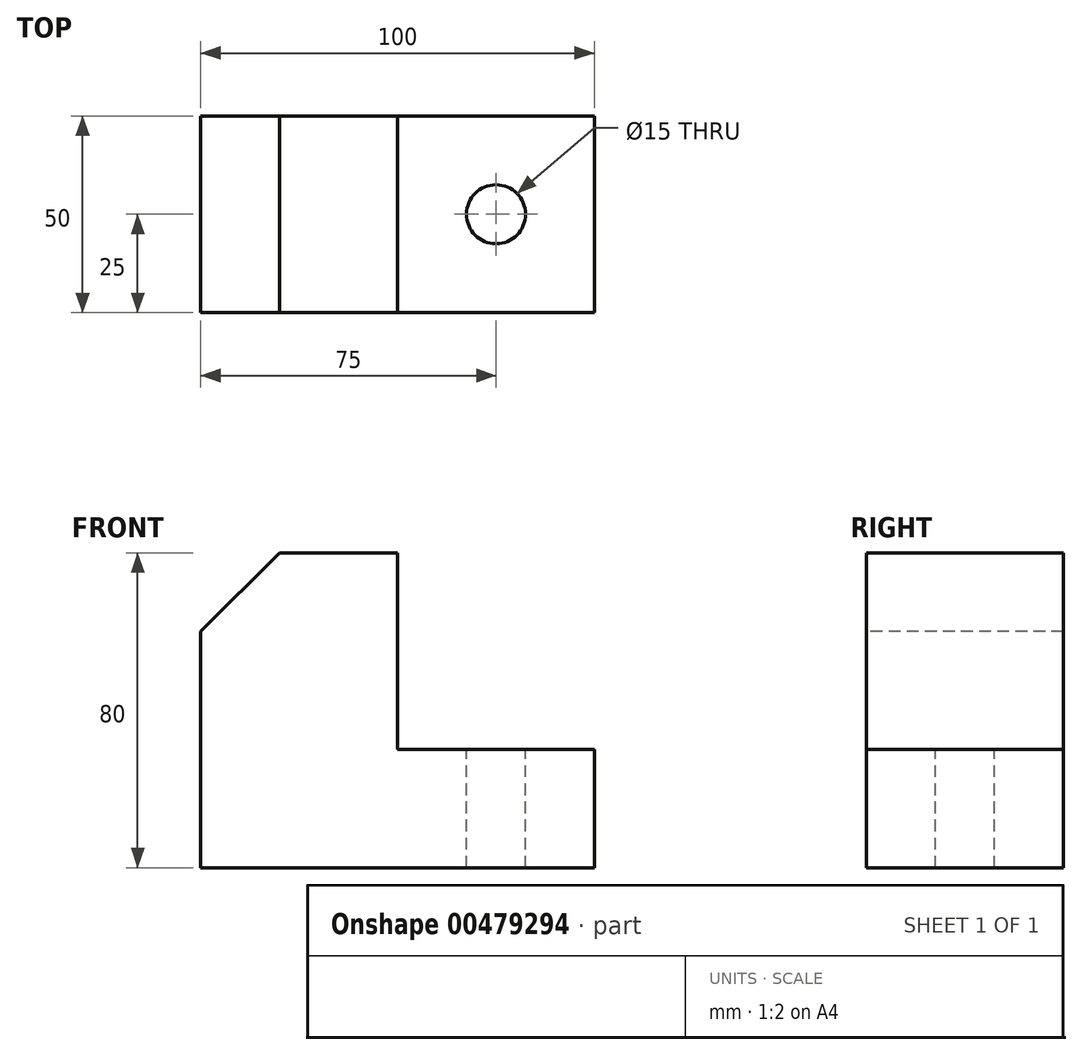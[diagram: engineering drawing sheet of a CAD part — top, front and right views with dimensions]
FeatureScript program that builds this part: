
annotation { "Feature Type Name" : "Feature", "Feature Type Description" : "" }
export const myFeature = defineFeature(function(context is Context, id is Id, definition is map)
    precondition{}
    {
        {
            var Q0;
            Q0=qCreatedBy(makeId("Top.planeOp"),FACE);
            var sketch = newSketch(context, id + "F0", { "sketchPlane" : qUnion([Q0])});
            skLineSegment(sketch, "E0.bottom", {"start": v(0, 0) * mm, "end": v(100, 0) * mm});
            skLineSegment(sketch, "E0.top", {"start": v(0, 50) * mm, "end": v(100, 50) * mm});
            skLineSegment(sketch, "E0.left", {"start": v(0, 0) * mm, "end": v(0, 50) * mm});
            skLineSegment(sketch, "E0.right", {"start": v(100, 0) * mm, "end": v(100, 50) * mm});
            skSolve(sketch);
        }
        {
            var Q0;
            Q0 = qSketchRegion(id + "F0", true);
            extrude(context, id + "F1", {"entities" : qUnion([Q0]), "depth" : 80 * mm});
        }
        {
            var Q0;
            Q0=makeQuery(id+"F1.opExtrude","CAP_FACE",FACE,{"disambiguationData":[OSD([sQuery(id+"F0.wireOp",EDGE,"E0.bottom"),sQuery(id+"F0.wireOp",EDGE,"E0.top"),sQuery(id+"F0.wireOp",EDGE,"E0.left"),sQuery(id+"F0.wireOp",EDGE,"E0.right")])],"isStart":false});
            var sketch = newSketch(context, id + "F2", { "sketchPlane" : qUnion([Q0])});
            skLineSegment(sketch, "E1.bottom", {"start": v(100, 0) * mm, "end": v(50, 0) * mm});
            skLineSegment(sketch, "E1.top", {"start": v(100, 50) * mm, "end": v(50, 50) * mm});
            skLineSegment(sketch, "E1.left", {"start": v(100, 0) * mm, "end": v(100, 50) * mm});
            skLineSegment(sketch, "E1.right", {"start": v(50, 0) * mm, "end": v(50, 50) * mm});
            skSolve(sketch);
        }
        {
            var Q0;
            Q0 = qSketchRegion(id + "F2", true);
            extrude(context, id + "F3", {"entities" : qUnion([Q0]), "operationType" : NewBodyOperationType.REMOVE, "oppositeDirection" : true, "depth" : 50 * mm});
        }
        {
            var Q0;
            Q0=makeQuery(id+"F3.boolean.opBoolean","COPY",FACE,{"derivedFrom":makeQuery(id+"F3.opExtrude","CAP_FACE",FACE,{"disambiguationData":[OSD([sQuery(id+"F2.wireOp",EDGE,"E1.bottom"),sQuery(id+"F2.wireOp",EDGE,"E1.top"),sQuery(id+"F2.wireOp",EDGE,"E1.left"),sQuery(id+"F2.wireOp",EDGE,"E1.right")])],"isStart":false})});
            var sketch = newSketch(context, id + "F4", { "sketchPlane" : qUnion([Q0])});
            skCircle(sketch, "E2", {"center": v(75, 25) * mm, "radius": 7.5 * mm});
            skSolve(sketch);
        }
        {
            var Q0;
            Q0 = qSketchRegion(id + "F4", true);
            extrude(context, id + "F5", {"entities" : qUnion([Q0]), "operationType" : NewBodyOperationType.REMOVE, "endBound" : BoundingType.THROUGH_ALL, "oppositeDirection" : true, "depth" : 25 * mm});
        }
        {
            var Q0;
            Q0=makeQuery(id+"F1.opExtrude","SWEPT_FACE",FACE,{"disambiguationData":[OSD([sQuery(id+"F0.wireOp",EDGE,"E0.bottom")])]});
            var sketch = newSketch(context, id + "F6", { "sketchPlane" : qUnion([Q0])});
            skLineSegment(sketch, "E3", {"start": v(0, 80) * mm, "end": v(20, 80) * mm});
            skLineSegment(sketch, "E4", {"start": v(0, 80) * mm, "end": v(0, 60) * mm});
            skLineSegment(sketch, "E5", {"start": v(20, 80) * mm, "end": v(0, 60) * mm});
            skSolve(sketch);
        }
        {
            var Q0;
            Q0 = qSketchRegion(id + "F6", true);
            extrude(context, id + "F7", {"entities" : qUnion([Q0]), "operationType" : NewBodyOperationType.REMOVE, "endBound" : BoundingType.THROUGH_ALL, "oppositeDirection" : true, "depth" : 25 * mm});
        }
    });
